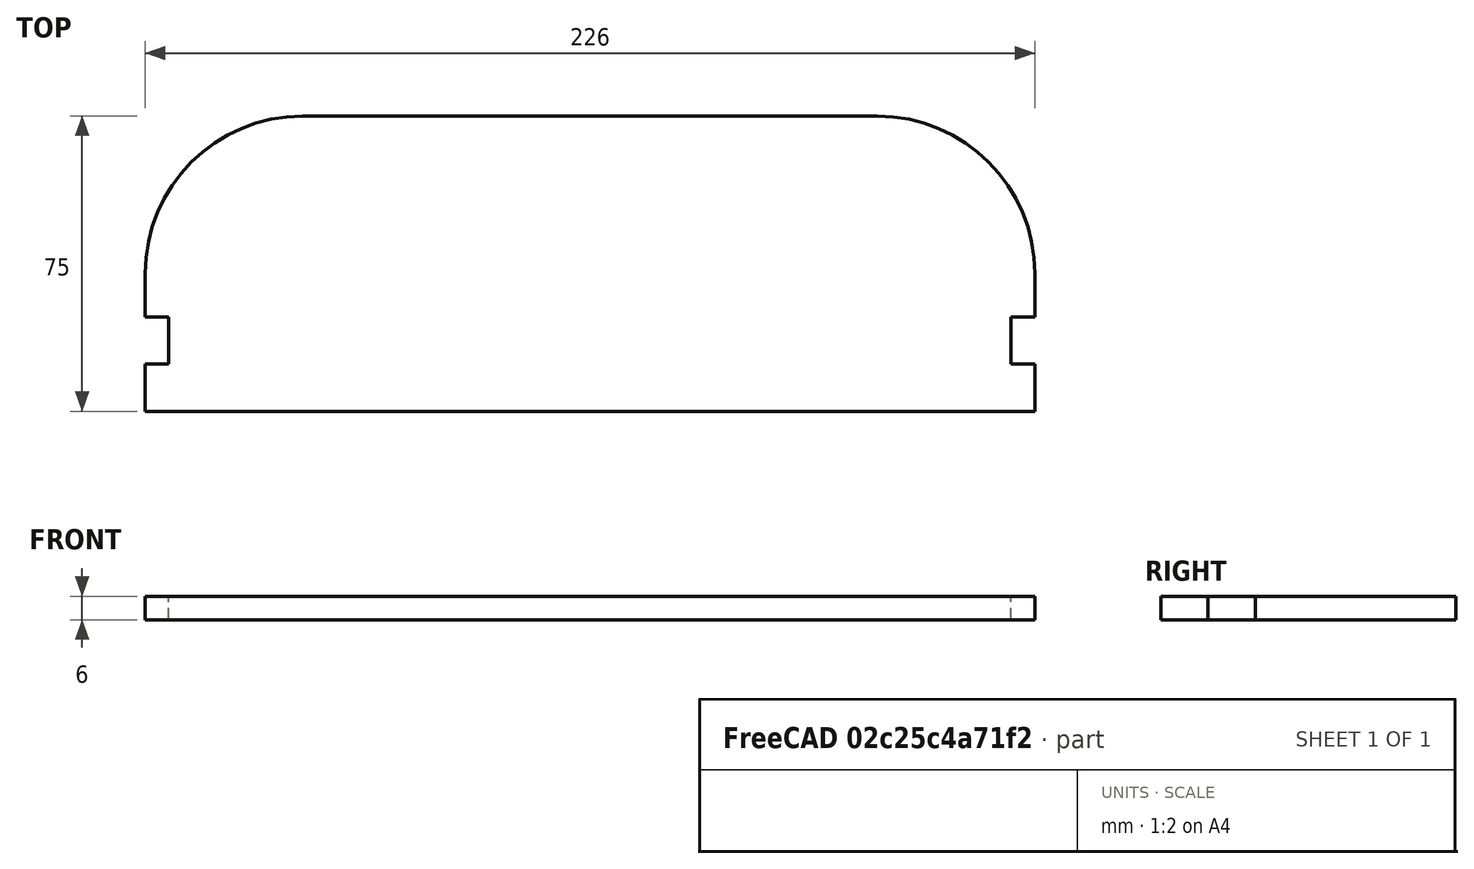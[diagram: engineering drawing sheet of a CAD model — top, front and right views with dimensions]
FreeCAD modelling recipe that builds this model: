
FCSTD DOCUMENT  (FreeCAD 0.16RUnknown)
Label: BASE_JUPE_MALE
License: All rights reserved
LicenseURL: http://en.wikipedia.org/wiki/All_rights_reserved
objects: Spreadsheet::Sheet×1, Sketcher::SketchObject×1, PartDesign::Pad×1
note: 3 computed .brp shape members not serialized (recipe doc carries the construction recipe); baked Part::Feature solids carry a one-line shape summary decoded from their .brp

FEATURE [Spreadsheet::Sheet] Spreadsheet  label="prefs"
  cells = A1=PCBHeated; B1(pcbheated)=214; C1=mm; D1=name=pcbheated; A2=Plexi thickness; B2(plexi)=6; C2=mm; D2=name=plexi
FEATURE [Sketcher::SketchObject] Sketch
  expr: Constraints[12] = prefs.pcbheated / 2 + prefs.plexi
  expr: Constraints[14] = prefs.plexi * 2
  expr: Constraints[17] = prefs.plexi * 2
  expr: Constraints[18] = prefs.plexi
  sketch-geometry (16):
    g0: LineSegment StartX=0 StartY=0 StartZ=0 EndX=113 EndY=0 EndZ=0
    g1: LineSegment StartX=113 StartY=0 StartZ=0 EndX=113 EndY=12 EndZ=0
    g2: LineSegment StartX=113 StartY=12 StartZ=0 EndX=107 EndY=12 EndZ=0
    g3: LineSegment StartX=107 StartY=12 StartZ=0 EndX=107 EndY=24 EndZ=0
    g4: LineSegment StartX=107 StartY=24 StartZ=0 EndX=113 EndY=24 EndZ=0
    g5: LineSegment StartX=113 StartY=24 StartZ=0 EndX=113 EndY=35 EndZ=0
    g6: LineSegment StartX=73 StartY=75 StartZ=0 EndX=0 EndY=75 EndZ=0
    g7: ArcOfCircle CenterX=73 CenterY=35 CenterZ=0 NormalX=0 NormalY=0 NormalZ=1 Radius=40 StartAngle=0 EndAngle=1.5708
    g8: LineSegment StartX=0 StartY=0 StartZ=0 EndX=-113 EndY=0 EndZ=0
    g9: LineSegment StartX=-113 StartY=0 StartZ=0 EndX=-113 EndY=12 EndZ=0
    g10: LineSegment StartX=-113 StartY=12 StartZ=0 EndX=-107 EndY=12 EndZ=0
    g11: LineSegment StartX=-107 StartY=12 StartZ=0 EndX=-107 EndY=24 EndZ=0
    g12: LineSegment StartX=-107 StartY=24 StartZ=0 EndX=-113 EndY=24 EndZ=0
    g13: LineSegment StartX=-113 StartY=24 StartZ=0 EndX=-113 EndY=35 EndZ=0
    g14: LineSegment StartX=-73 StartY=75 StartZ=0 EndX=0 EndY=75 EndZ=0
    g15: ArcOfCircle CenterX=-73 CenterY=35 CenterZ=0 NormalX=0 NormalY=0 NormalZ=1 Radius=40 StartAngle=1.5708 EndAngle=3.14159
  constraints (45):
    c: Coincident(g0,g-1)
    c: Horizontal(g0)
    c: Coincident(g1,g0)
    c: Vertical(g1)
    c: Horizontal(g2)
    c: Vertical(g3)
    c: Horizontal(g4)
    c: Vertical(g5)
    c: PointOnObject(g6,g-2)
    c: Horizontal(g6)
    c: Tangent(g6,g7) = -1.5708
    c: Tangent(g5,g7) = -1.5708
    c: DistanceX(g0,g0) = 113
    c: Coincident(g2,g1)
    c: DistanceY(g1,g1) = 12
    c: Coincident(g3,g4)
    c: Coincident(g3,g2)
    c: DistanceY(g3,g3) = 12
    c: DistanceX(g2,g2) = 6
    c: Coincident(g4,g5)
    c: Equal(g4,g2)
    c: Radius(g7) = 40
    c: DistanceY(g-1,g6) = 75
    c: Horizontal(g8)
    c: Coincident(g9,g8)
    c: Vertical(g9)
    c: Horizontal(g10)
    c: Vertical(g11)
    c: Horizontal(g12)
    c: Vertical(g13)
    c: Horizontal(g14)
    c: Tangent(g14,g15) = 1.5708
    c: Tangent(g13,g15) = 1.5708
    c: Coincident(g10,g9)
    c: Coincident(g11,g12)
    c: Coincident(g11,g10)
    c: Coincident(g12,g13)
    c: Equal(g12,g10)
    c: Radius(g15) = 40
    c: DistanceX(g8,g8) = 113
    c: DistanceY(g9,g9) = 12
    c: DistanceY(g11,g11) = 12
    c: DistanceX(g10,g10) = 6
    c: Coincident(g14,g6)
    c: Coincident(g8,g-1)
FEATURE [PartDesign::Pad] Pad
  Length = 6
  Length2 = 100
  Sketch = -> Sketch
  Type = 0
